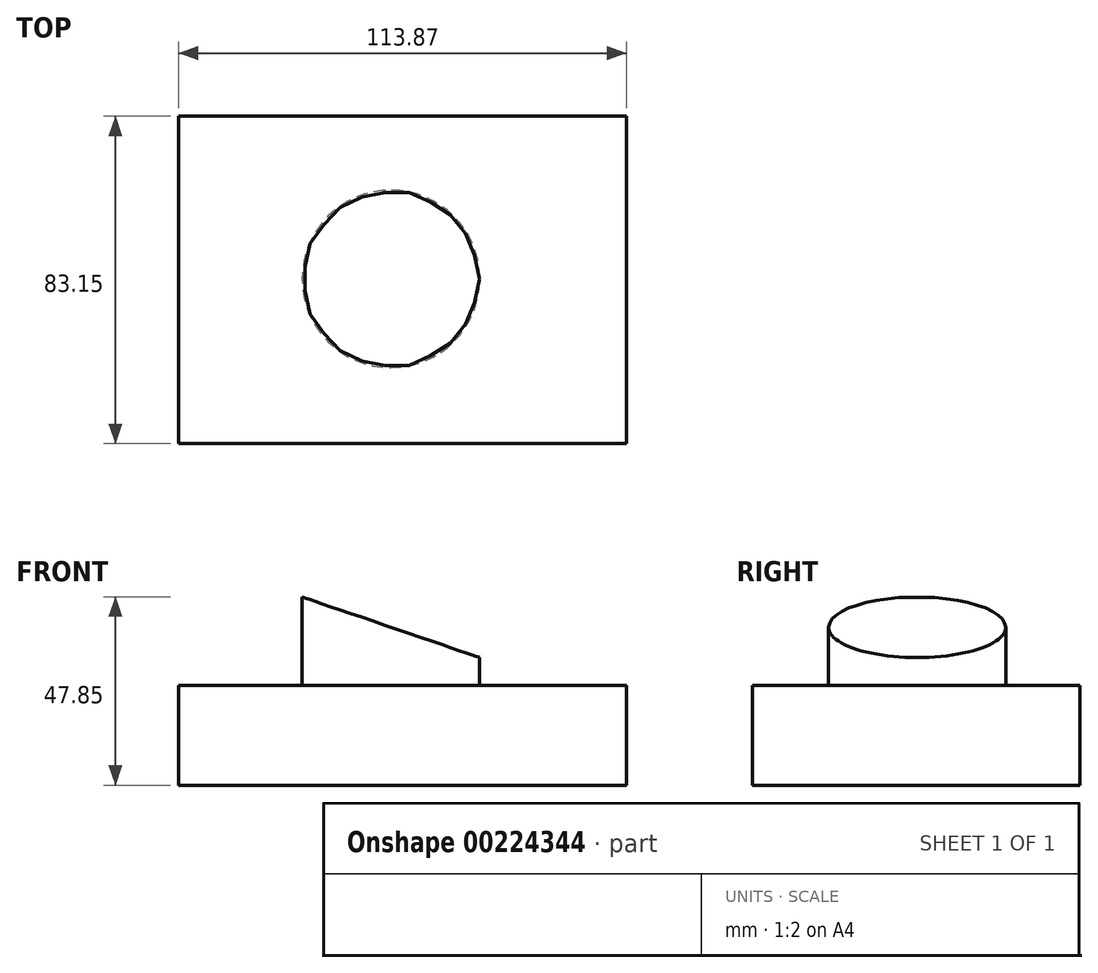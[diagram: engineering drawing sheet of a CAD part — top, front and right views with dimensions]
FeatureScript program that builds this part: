
annotation { "Feature Type Name" : "Feature", "Feature Type Description" : "" }
export const myFeature = defineFeature(function(context is Context, id is Id, definition is map)
    precondition{}
    {
        {
            var Q0;
            Q0=qCreatedBy(makeId("Top.planeOp"),FACE);
            var sketch = newSketch(context, id + "F0", { "sketchPlane" : qUnion([Q0])});
            skLineSegment(sketch, "E0.bottom", {"start": v(0, 0) * mm, "end": v(-113.87, 0) * mm});
            skLineSegment(sketch, "E0.top", {"start": v(0, 83.15) * mm, "end": v(-113.87, 83.15) * mm});
            skLineSegment(sketch, "E0.left", {"start": v(0, 0) * mm, "end": v(0, 83.15) * mm});
            skLineSegment(sketch, "E0.right", {"start": v(-113.87, 0) * mm, "end": v(-113.87, 83.15) * mm});
            skSolve(sketch);
        }
        {
            var Q0;
            Q0 = qSketchRegion(id + "F0", true);
            extrude(context, id + "F1", {"entities" : qUnion([Q0]), "depth" : 25.4 * mm});
        }
        {
            var Q0;
            Q0=makeQuery(id+"F1.opExtrude","CAP_FACE",FACE,{"disambiguationData":[OSD([sQuery(id+"F0.wireOp",EDGE,"E0.bottom"),sQuery(id+"F0.wireOp",EDGE,"E0.top"),sQuery(id+"F0.wireOp",EDGE,"E0.left"),sQuery(id+"F0.wireOp",EDGE,"E0.right")])],"isStart":false});
            var sketch = newSketch(context, id + "F2", { "sketchPlane" : qUnion([Q0])});
            skCircle(sketch, "E1", {"center": v(-59.87, 41.8) * mm, "radius": 22.54 * mm});
            skSolve(sketch);
        }
        {
            var Q0;
            Q0 = qSketchRegion(id + "F2", true);
            extrude(context, id + "F3", {"entities" : qUnion([Q0]), "operationType" : NewBodyOperationType.ADD, "depth" : 25.4 * mm});
        }
        {
            var Q0;
            Q0=qCreatedBy(makeId("Front.planeOp"),FACE);
            var sketch = newSketch(context, id + "F4", { "sketchPlane" : qUnion([Q0])});
            skLineSegment(sketch, "E2", {"start": v(-86.74, 49.33) * mm, "end": v(-32, 30.64) * mm});
            skLineSegment(sketch, "E3", {"start": v(-32, 30.64) * mm, "end": v(-32, 64.94) * mm});
            skLineSegment(sketch, "E4", {"start": v(-32, 64.94) * mm, "end": v(-102.13, 49.1) * mm});
            skLineSegment(sketch, "E5", {"start": v(-86.74, 49.33) * mm, "end": v(-102.13, 49.1) * mm});
            skSolve(sketch);
        }
        {
            var Q0;
            Q0=makeQuery(id+"F4.imprint","IMPRINT",FACE,{"disambiguationData":[TD([[makeQuery(id+"F4.imprint","IMPRINT",EDGE,{"derivedFrom":sQuery(id+"F4.wireOp",EDGE,"E2")}),1.0]])]});
            extrude(context, id + "F5", {"entities" : qUnion([Q0]), "operationType" : NewBodyOperationType.REMOVE, "oppositeDirection" : true, "depth" : 76.2 * mm});
        }
    });
